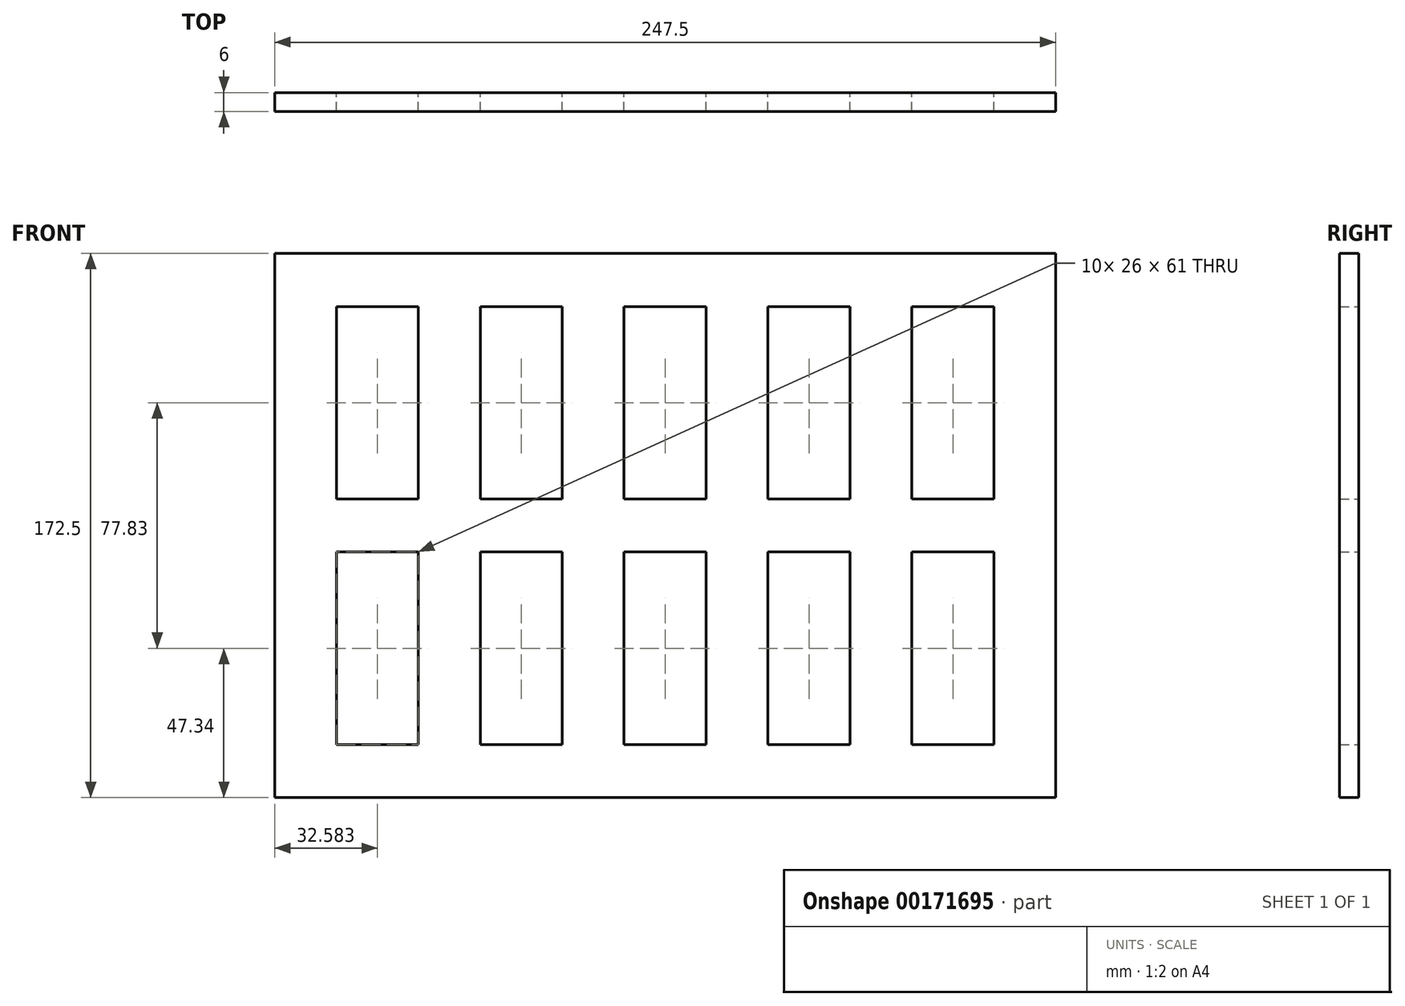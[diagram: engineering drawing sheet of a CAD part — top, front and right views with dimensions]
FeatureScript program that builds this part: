
annotation { "Feature Type Name" : "Feature", "Feature Type Description" : "" }
export const myFeature = defineFeature(function(context is Context, id is Id, definition is map)
    precondition{}
    {
        {
            var Q0;
            Q0=qCreatedBy(makeId("Front.planeOp"),FACE);
            var sketch = newSketch(context, id + "F0", { "sketchPlane" : qUnion([Q0])});
            skLineSegment(sketch, "E0.bottom", {"start": v(123.75, -86.25) * mm, "end": v(-123.75, -86.25) * mm});
            skLineSegment(sketch, "E0.top", {"start": v(123.75, 86.25) * mm, "end": v(-123.75, 86.25) * mm});
            skLineSegment(sketch, "E0.left", {"start": v(123.75, -86.25) * mm, "end": v(123.75, 86.25) * mm});
            skLineSegment(sketch, "E0.right", {"start": v(-123.75, -86.25) * mm, "end": v(-123.75, 86.25) * mm});
            skPoint(sketch, "E0.middle", {"position": v(0, 0) * mm});
            skLineSegment(sketch, "E1.bottom", {"start": v(-78.17, 8.42) * mm, "end": v(-104.17, 8.42) * mm});
            skLineSegment(sketch, "E1.top", {"start": v(-78.17, 69.42) * mm, "end": v(-104.17, 69.42) * mm});
            skLineSegment(sketch, "E1.left", {"start": v(-78.17, 8.42) * mm, "end": v(-78.17, 69.42) * mm});
            skLineSegment(sketch, "E1.right", {"start": v(-104.17, 8.42) * mm, "end": v(-104.17, 69.42) * mm});
            skPoint(sketch, "E1.middle", {"position": v(-91.17, 38.92) * mm});
            skLineSegment(sketch, "E2.0.1.0", {"start": v(-104.17, -69.4) * mm, "end": v(-104.17, -8.4) * mm});
            skLineSegment(sketch, "E2.0.1.1", {"start": v(-78.17, -8.4) * mm, "end": v(-104.17, -8.4) * mm});
            skLineSegment(sketch, "E2.0.1.2", {"start": v(-78.17, -69.4) * mm, "end": v(-78.17, -8.4) * mm});
            skLineSegment(sketch, "E2.0.1.3", {"start": v(-78.17, -69.4) * mm, "end": v(-104.17, -69.4) * mm});
            skLineSegment(sketch, "E2.1.0.0", {"start": v(-58.58, 8.42) * mm, "end": v(-58.58, 69.42) * mm});
            skLineSegment(sketch, "E2.1.0.1", {"start": v(-32.58, 69.42) * mm, "end": v(-58.58, 69.42) * mm});
            skLineSegment(sketch, "E2.1.0.2", {"start": v(-32.58, 8.42) * mm, "end": v(-32.58, 69.42) * mm});
            skLineSegment(sketch, "E2.1.0.3", {"start": v(-32.58, 8.42) * mm, "end": v(-58.58, 8.42) * mm});
            skLineSegment(sketch, "E2.1.1.0", {"start": v(-58.58, -69.4) * mm, "end": v(-58.58, -8.4) * mm});
            skLineSegment(sketch, "E2.1.1.1", {"start": v(-32.58, -8.4) * mm, "end": v(-58.58, -8.4) * mm});
            skLineSegment(sketch, "E2.1.1.2", {"start": v(-32.58, -69.4) * mm, "end": v(-32.58, -8.4) * mm});
            skLineSegment(sketch, "E2.1.1.3", {"start": v(-32.58, -69.4) * mm, "end": v(-58.58, -69.4) * mm});
            skLineSegment(sketch, "E2.2.0.0", {"start": v(-13, 8.42) * mm, "end": v(-13, 69.42) * mm});
            skLineSegment(sketch, "E2.2.0.1", {"start": v(13, 69.42) * mm, "end": v(-13, 69.42) * mm});
            skLineSegment(sketch, "E2.2.0.2", {"start": v(13, 8.42) * mm, "end": v(13, 69.42) * mm});
            skLineSegment(sketch, "E2.2.0.3", {"start": v(13, 8.42) * mm, "end": v(-13, 8.42) * mm});
            skLineSegment(sketch, "E2.2.1.0", {"start": v(-13, -69.4) * mm, "end": v(-13, -8.4) * mm});
            skLineSegment(sketch, "E2.2.1.1", {"start": v(13, -8.4) * mm, "end": v(-13, -8.4) * mm});
            skLineSegment(sketch, "E2.2.1.2", {"start": v(13, -69.4) * mm, "end": v(13, -8.4) * mm});
            skLineSegment(sketch, "E2.2.1.3", {"start": v(13, -69.4) * mm, "end": v(-13, -69.4) * mm});
            skLineSegment(sketch, "E2.3.0.0", {"start": v(32.58, 8.42) * mm, "end": v(32.58, 69.42) * mm});
            skLineSegment(sketch, "E2.3.0.1", {"start": v(58.58, 69.42) * mm, "end": v(32.58, 69.42) * mm});
            skLineSegment(sketch, "E2.3.0.2", {"start": v(58.58, 8.42) * mm, "end": v(58.58, 69.42) * mm});
            skLineSegment(sketch, "E2.3.0.3", {"start": v(58.58, 8.42) * mm, "end": v(32.58, 8.42) * mm});
            skLineSegment(sketch, "E2.3.1.0", {"start": v(32.58, -69.4) * mm, "end": v(32.58, -8.4) * mm});
            skLineSegment(sketch, "E2.3.1.1", {"start": v(58.58, -8.4) * mm, "end": v(32.58, -8.4) * mm});
            skLineSegment(sketch, "E2.3.1.2", {"start": v(58.58, -69.4) * mm, "end": v(58.58, -8.4) * mm});
            skLineSegment(sketch, "E2.3.1.3", {"start": v(58.58, -69.4) * mm, "end": v(32.58, -69.4) * mm});
            skLineSegment(sketch, "E2.4.0.0", {"start": v(78.17, 8.42) * mm, "end": v(78.17, 69.42) * mm});
            skLineSegment(sketch, "E2.4.0.1", {"start": v(104.17, 69.42) * mm, "end": v(78.17, 69.42) * mm});
            skLineSegment(sketch, "E2.4.0.2", {"start": v(104.17, 8.42) * mm, "end": v(104.17, 69.42) * mm});
            skLineSegment(sketch, "E2.4.0.3", {"start": v(104.17, 8.42) * mm, "end": v(78.17, 8.42) * mm});
            skLineSegment(sketch, "E2.4.1.0", {"start": v(78.17, -69.4) * mm, "end": v(78.17, -8.4) * mm});
            skLineSegment(sketch, "E2.4.1.1", {"start": v(104.17, -8.4) * mm, "end": v(78.17, -8.4) * mm});
            skLineSegment(sketch, "E2.4.1.2", {"start": v(104.17, -69.4) * mm, "end": v(104.17, -8.4) * mm});
            skLineSegment(sketch, "E2.4.1.3", {"start": v(104.17, -69.4) * mm, "end": v(78.17, -69.4) * mm});
            skLineSegment(sketch, "E2.direction1", {"start": v(-104.17, 8.42) * mm, "end": v(-58.58, 8.42) * mm, "construction": true});
            skLineSegment(sketch, "E2.direction2", {"start": v(-104.17, 8.42) * mm, "end": v(-104.17, -69.4) * mm, "construction": true});
            skSolve(sketch);
        }
        {
            var Q0;
            Q0 = qSketchRegion(id + "F0", true);
            extrude(context, id + "F1", {"entities" : qUnion([Q0]), "depth" : 6 * mm, "offsetDistance" : 25 * mm});
        }
    });
